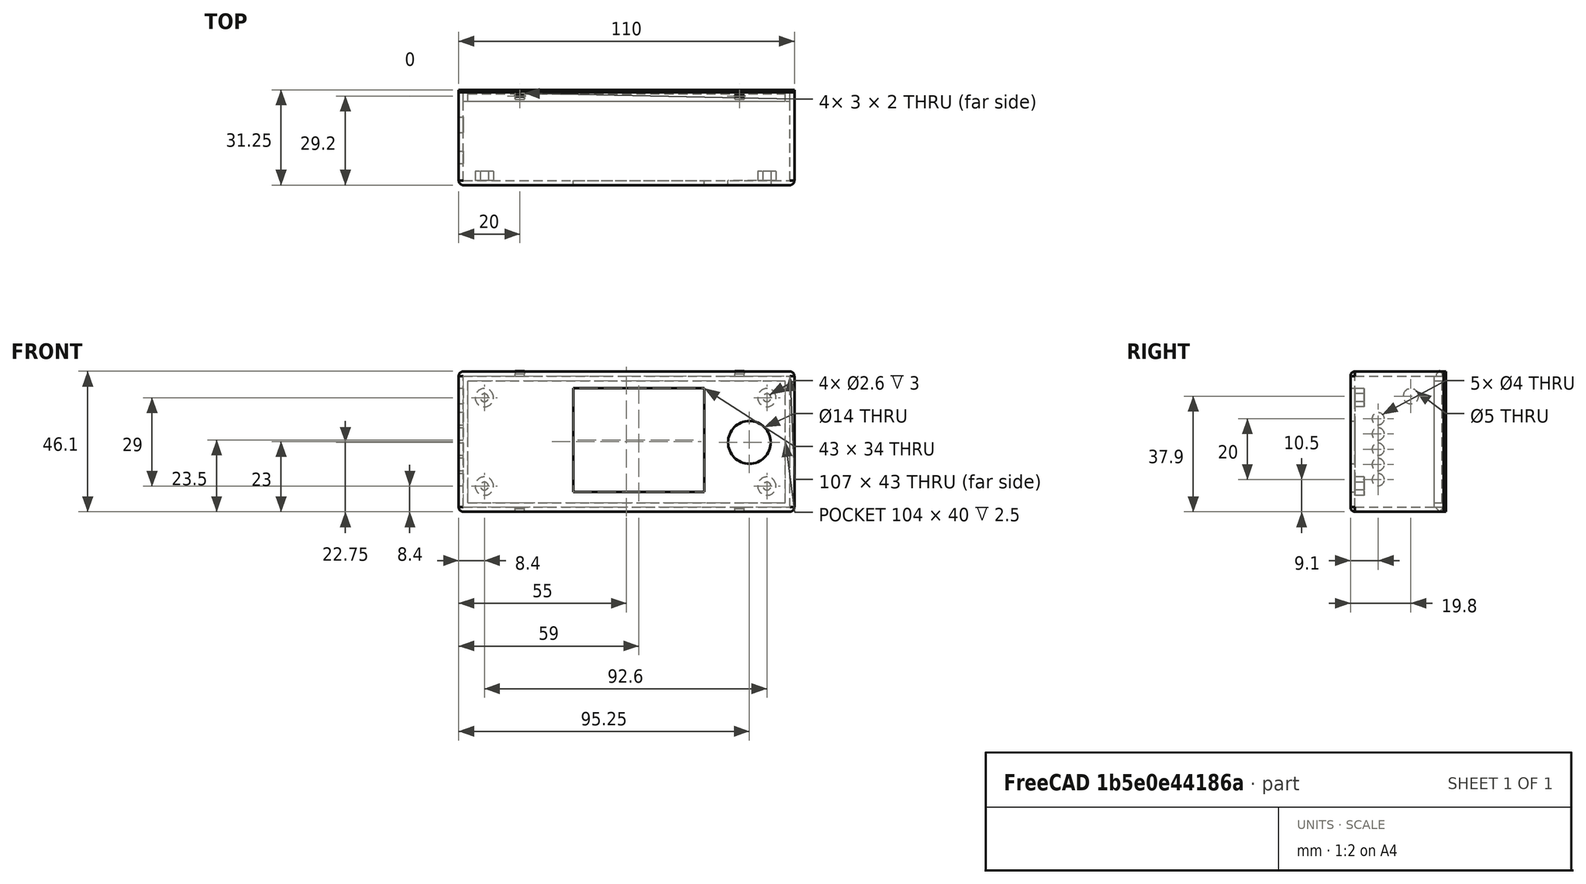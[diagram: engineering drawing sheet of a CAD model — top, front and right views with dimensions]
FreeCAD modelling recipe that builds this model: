
FCSTD DOCUMENT  (FreeCAD 1.0R39285 (Git))
Label: Plataforma_soldadora_caixa_1
License: All rights reserved
LicenseURL: https://en.wikipedia.org/wiki/All_rights_reserved
objects: Part::Box×9, Part::Cylinder×7, Part::MultiFuse×7, Part::Cut×6, Part::Chamfer×4, Part::FeaturePython×4, Mesh::Feature×2, Part::Thickness×1, Part::Fillet×1
note: 39 computed .brp shape members not serialized (recipe doc carries the construction recipe); baked Part::Feature solids carry a one-line shape summary decoded from their .brp

FEATURE [Mesh::Feature] Plataforma_soldadora
  Placement = pos=(3,5,3) rot=(1,0,0;1.5708rad)
FEATURE [Part::Box] Box  label="Cubo"
  AttacherType = Attacher::AttachEngine3D
  Height = 43
  Length = 107
  Width = 29
FEATURE [Part::Box] Box001  label="Cubo001"
  AttacherType = Attacher::AttachEngine3D
  Height = 34
  Length = 43
  Placement = pos=(36,-1,5) rot=(0,0,1;0rad)
  Width = 10
FEATURE [Part::Cylinder] Cylinder001  label="Cilindro001"
  Angle = 360
  AttacherType = Attacher::AttachEngine3D
  FirstAngle = 0
  Height = 10
  Placement = pos=(93.75,1,21.25) rot=(1,0,0;1.5708rad)
  Radius = 7
  SecondAngle = 0
FEATURE [Mesh::Feature] _55SB  label="255SB"
  Placement = pos=(-12.4,14.5,37.4) rot=(0,-1,0;1.5708rad)
FEATURE [Part::Cylinder] Cylinder005  label="Cilindro005"
  Angle = 360
  AttacherType = Attacher::AttachEngine3D
  FirstAngle = 0
  Height = 10
  Placement = pos=(3,19.3,36.4) rot=(0,1,0;4.71239rad)
  Radius = 2.5
  SecondAngle = 0
FEATURE [Part::Thickness] Thickness
  Faces = -> Box [Face4]
  Intersection = false
  Join = 0
  Mode = 0
  Placement = pos=(0,1,0) rot=(0,0,1;0rad)
  SelfIntersection = false
  Value = 1.5
FEATURE [Part::Cut] Cut
  Base = -> Thickness
  Refine = true
  Tool = -> Box001
FEATURE [Part::Cut] Cut001
  Base = -> Cut
  Refine = true
  Tool = -> Cylinder001
FEATURE [Part::Cut] Cut002
  Base = -> Cut001
  Refine = true
  Tool = -> Cylinder005
FEATURE [Part::Box] Box025  label="Cubo025"
  AttacherType = Attacher::AttachEngine3D
  Height = 2
  Length = 3
  Placement = pos=(5,-1,-6) rot=(0,0,1;0rad)
  Width = 46
FEATURE [Part::Chamfer] Chamfer
  Base = -> Box025
  EdgeLinks = -> Box025 [Edge9,Edge10,Edge11,Edge12]
  Edges = 4 edges r=0.9: [Edge9,Edge10,Edge11,Edge12]
  Placement = pos=(12,23.7,-0.4) rot=(1,0,0;1.5708rad)
FEATURE [Part::Box] Box026  label="Cubo026"
  AttacherType = Attacher::AttachEngine3D
  Height = 2
  Length = 3
  Placement = pos=(5,-1,-6) rot=(0,0,1;0rad)
  Width = 46
FEATURE [Part::Chamfer] Chamfer001
  Base = -> Box026
  EdgeLinks = -> Box026 [Edge9,Edge10,Edge11,Edge12]
  Edges = 4 edges r=0.9: [Edge9,Edge10,Edge11,Edge12]
  Placement = pos=(84,23.7,-0.4) rot=(1,0,0;1.5708rad)
FEATURE [Part::MultiFuse] Fusion
  Refine = true
  Shapes = -> [Chamfer,Chamfer001]
FEATURE [Part::Box] Box027  label="Cubo027"
  AttacherType = Attacher::AttachEngine3D
  Height = 2
  Length = 3
  Placement = pos=(5,-1,-6) rot=(0,0,1;0rad)
  Width = 46
FEATURE [Part::Box] Box028  label="Cubo028"
  AttacherType = Attacher::AttachEngine3D
  Height = 2
  Length = 3
  Placement = pos=(5,-1,-6) rot=(0,0,1;0rad)
  Width = 46
FEATURE [Part::Chamfer] Chamfer002
  Base = -> Box027
  EdgeLinks = -> Box027 [Edge9,Edge10,Edge11,Edge12]
  Edges = 4 edges r=0.9: [Edge9,Edge10,Edge11,Edge12]
  Placement = pos=(12,23.7,-0.4) rot=(1,0,0;1.5708rad)
FEATURE [Part::Chamfer] Chamfer003
  Base = -> Box028
  EdgeLinks = -> Box028 [Edge9,Edge10,Edge11,Edge12]
  Edges = 4 edges r=0.9: [Edge9,Edge10,Edge11,Edge12]
  Placement = pos=(84,23.7,-0.4) rot=(1,0,0;1.5708rad)
FEATURE [Part::MultiFuse] Fusion001
  Refine = true
  Shapes = -> [Chamfer002,Chamfer003]
FEATURE [Part::Cut] Cut003
  Base = -> Cut002
  Refine = true
  Tool = -> Fusion
FEATURE [Part::Box] Box029  label="Cubo029"
  AttacherType = Attacher::AttachEngine3D
  Height = 43
  Length = 107
  Placement = pos=(0,27,0) rot=(0,0,1;0rad)
  Width = 3
FEATURE [Part::MultiFuse] Fusion002
  Refine = true
  Shapes = -> [Fusion001,Box029]
FEATURE [Part::Box] Box030  label="Cubo030"
  AttacherType = Attacher::AttachEngine3D
  Height = 40
  Length = 104
  Placement = pos=(1.5,27,1.5) rot=(0,0,1;0rad)
  Width = 2.5
FEATURE [Part::Cut] Cut004
  Base = -> Fusion002
  Refine = true
  Tool = -> Box030
FEATURE [Part::Box] Box031  label="Cubo031"
  AttacherType = Attacher::AttachEngine3D
  Height = 46
  Length = 110
  Placement = pos=(-1.5,30,-1.5) rot=(0,0,1;0rad)
  Width = 0.75
FEATURE [Part::Fillet] Fillet
  Base = -> Box031
  EdgeLinks = -> Box031 [Edge2,Edge4,Edge6,Edge8]
  Edges = 4 edges r=1.5: [Edge2,Edge4,Edge6,Edge8]
FEATURE [Part::MultiFuse] Fusion003  label="Tapa"
  Refine = true
  Shapes = -> [Fillet,Cut004]
FEATURE [Part::Cylinder] Cylinder006  label="Cilindro006"
  Angle = 360
  AttacherType = Attacher::AttachEngine3D
  FirstAngle = 0
  Height = 10
  Placement = pos=(5.4,8.6,29) rot=(0,1,0;4.71239rad)
  Radius = 2
  SecondAngle = 0
FEATURE [Part::Cylinder] Cylinder007  label="Cilindro007"
  Angle = 360
  AttacherType = Attacher::AttachEngine3D
  FirstAngle = 0
  Height = 10
  Placement = pos=(5.4,8.6,24) rot=(0,1,0;4.71239rad)
  Radius = 2
  SecondAngle = 0
FEATURE [Part::Cylinder] Cylinder008  label="Cilindro008"
  Angle = 360
  AttacherType = Attacher::AttachEngine3D
  FirstAngle = 0
  Height = 10
  Placement = pos=(5.4,8.6,19) rot=(0,1,0;4.71239rad)
  Radius = 2
  SecondAngle = 0
FEATURE [Part::Cylinder] Cylinder009  label="Cilindro009"
  Angle = 360
  AttacherType = Attacher::AttachEngine3D
  FirstAngle = 0
  Height = 10
  Placement = pos=(5.4,8.6,14) rot=(0,1,0;4.71239rad)
  Radius = 2
  SecondAngle = 0
FEATURE [Part::Cylinder] Cylinder010  label="Cilindro010"
  Angle = 360
  AttacherType = Attacher::AttachEngine3D
  FirstAngle = 0
  Height = 10
  Placement = pos=(5.4,8.6,9) rot=(0,1,0;4.71239rad)
  Radius = 2
  SecondAngle = 0
FEATURE [Part::MultiFuse] Fusion004
  Refine = true
  Shapes = -> [Cylinder006,Cylinder007,Cylinder008,Cylinder009,Cylinder010]
FEATURE [Part::Cut] Cut005
  Base = -> Cut003
  Refine = true
  Tool = -> Fusion004
FEATURE [Part::FeaturePython] Tube  # WARN: FeaturePython — macro-defined, semantics opaque (R4)
  AttacherType = Attacher::AttachEngine3D
  Height = 4
  InnerRadius = 1.3
  OuterRadius = 3
  Placement = pos=(6.9,4,6.9) rot=(1,0,0;1.5708rad)
FEATURE [Part::FeaturePython] Tube001  # WARN: FeaturePython — macro-defined, semantics opaque (R4)
  AttacherType = Attacher::AttachEngine3D
  Height = 4
  InnerRadius = 1.3
  OuterRadius = 3
  Placement = pos=(6.9,4,35.9) rot=(1,0,0;1.5708rad)
FEATURE [Part::FeaturePython] Tube002  # WARN: FeaturePython — macro-defined, semantics opaque (R4)
  AttacherType = Attacher::AttachEngine3D
  Height = 4
  InnerRadius = 1.3
  OuterRadius = 3
  Placement = pos=(99.5,4,6.9) rot=(1,0,0;1.5708rad)
FEATURE [Part::FeaturePython] Tube003  # WARN: FeaturePython — macro-defined, semantics opaque (R4)
  AttacherType = Attacher::AttachEngine3D
  Height = 4
  InnerRadius = 1.3
  OuterRadius = 3
  Placement = pos=(99.5,4,35.9) rot=(1,0,0;1.5708rad)
FEATURE [Part::MultiFuse] Fusion005
  Refine = true
  Shapes = -> [Tube,Tube001,Tube002,Tube003]
FEATURE [Part::MultiFuse] Fusion006  label="Caixa"
  Refine = true
  Shapes = -> [Cut005,Fusion005]
